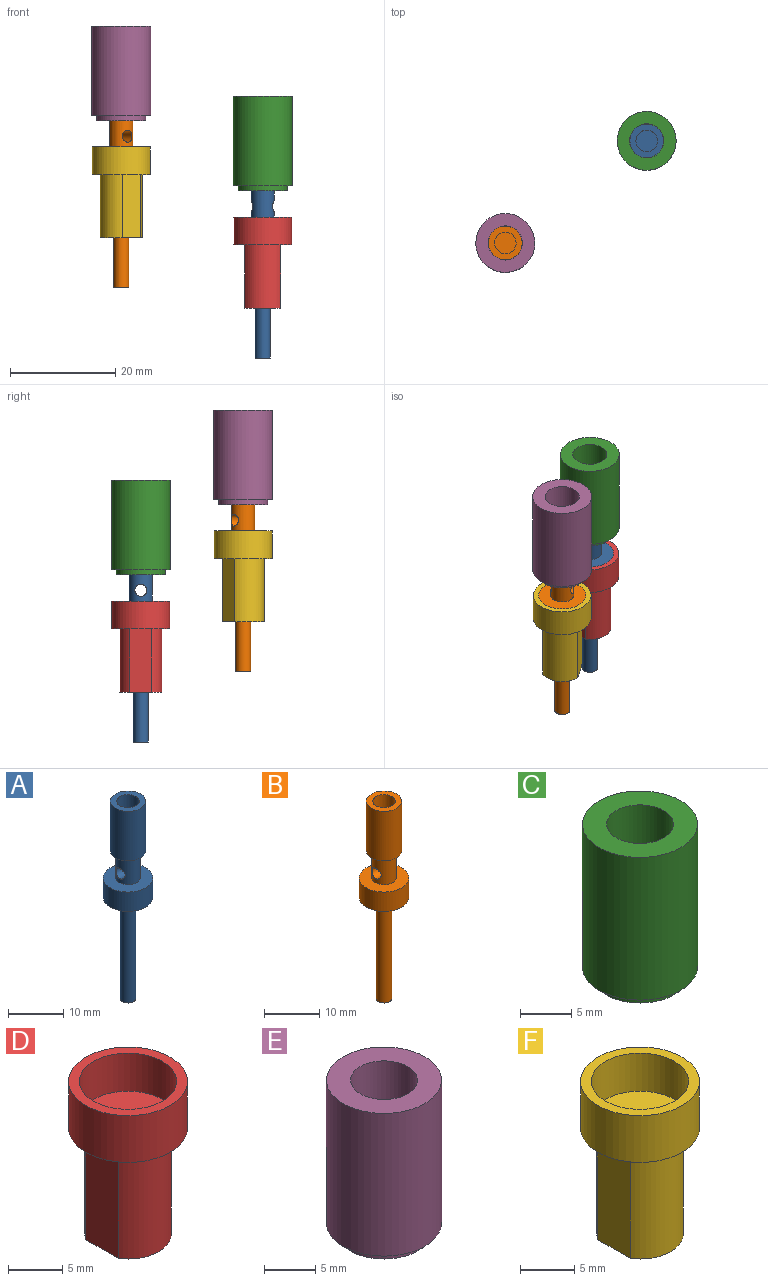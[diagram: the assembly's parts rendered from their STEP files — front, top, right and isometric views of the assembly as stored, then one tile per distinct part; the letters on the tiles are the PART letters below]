
ASSEMBLY  parts=6 mates=4
PART A: 12 faces, bbox 9x9x43.8 mm
  f0: plane 9x9mm, normal (0,0,1), area 48.4mm2, adj f1,f2
  f1: cylinder r=4.5mm len=9mm, axis (0,0,-1), area 121.6mm2, adj f0,f7
  f2: cylinder r=2.2mm len=6mm, axis (0,0,-1), area 74.3mm2, adj f0,f5,f9
  f3: cylinder r=3.2mm len=11mm, axis (0,0,-1), area 221.2mm2, adj f4,f5
  f4: plane 6.4x6.4mm, normal (0,0,1), area 19mm2, adj f3,f10
  f5: plane 6.4x6.4mm, normal (0,0,-1), area 17mm2, adj f2,f3
  f6: cylinder r=1.43mm len=22.5mm, axis (0,0,-1), area 201.5mm2, adj f7,f8
  f7: plane 9x9mm, normal (0,0,-1), area 57.2mm2, adj f1,f6
  f8: plane 2.85x2.85mm, normal (0,0,-1), area 6.4mm2, adj f6
  f9: cylinder r=1.15mm len=4.4mm, axis (1,0,0), area 29.5mm2, adj f2
  f10: cylinder r=2.05mm len=10mm, axis (0,0,1), area 128.8mm2, adj f4,f11
  f11: plane 4.1x4.1mm, normal (0,0,1), area 13.2mm2, adj f10
PART B: 12 faces, bbox 9x9x43.8 mm
  f0: plane 9x9mm, normal (0,0,1), area 48.4mm2, adj f1,f2
  f1: cylinder r=4.5mm len=9mm, axis (0,0,-1), area 121.6mm2, adj f0,f7
  f2: cylinder r=2.2mm len=6mm, axis (0,0,-1), area 74.3mm2, adj f0,f5,f9
  f3: cylinder r=3.2mm len=11mm, axis (0,0,-1), area 221.2mm2, adj f4,f5
  f4: plane 6.4x6.4mm, normal (0,0,1), area 19mm2, adj f3,f10
  f5: plane 6.4x6.4mm, normal (0,0,-1), area 17mm2, adj f2,f3
  f6: cylinder r=1.43mm len=22.5mm, axis (0,0,-1), area 201.5mm2, adj f7,f8
  f7: plane 9x9mm, normal (0,0,-1), area 57.2mm2, adj f1,f6
  f8: plane 2.85x2.85mm, normal (0,0,-1), area 6.4mm2, adj f6
  f9: cylinder r=1.15mm len=4.4mm, axis (1,0,0), area 29.5mm2, adj f2
  f10: cylinder r=2.05mm len=10mm, axis (0,0,1), area 128.8mm2, adj f4,f11
  f11: plane 4.1x4.1mm, normal (0,0,1), area 13.2mm2, adj f10
PART C: 8 faces, bbox 11.2x11.2x18 mm
  f0: plane 6.5x6.5mm, normal (0,0,1), area 18mm2, adj f1,f6
  f1: cylinder r=2.2mm len=4.4mm, axis (0,0,-1), area 13.8mm2, adj f0,f3
  f2: cylinder r=4.68mm len=9.35mm, axis (0,0,-1), area 29.4mm2, adj f3,f4
  f3: plane 9.35x9.35mm, normal (0,0,-1), area 53.5mm2, adj f1,f2
  f4: plane 11.2x11.2mm, normal (0,0,-1), area 29.9mm2, adj f2,f5
  f5: cylinder r=5.6mm len=17mm, axis (0,0,-1), area 598.2mm2, adj f4,f7
  f6: cylinder r=3.25mm len=17mm, axis (0,0,-1), area 347.1mm2, adj f0,f7
  f7: plane 11.2x11.2mm, normal (0,0,1), area 65.3mm2, adj f5,f6
PART D: 11 faces, bbox 11x11x17.3 mm
  f0: plane 11x11mm, normal (0,0,-1), area 48.2mm2, adj f2,f6,f7,f8,f9
  f1: cylinder r=4.5mm len=9mm, axis (0,0,-1), area 121.6mm2, adj f3,f5
  f2: cylinder r=5.5mm len=11mm, axis (0,0,-1), area 183.2mm2, adj f0,f3
  f3: plane 11x11mm, normal (0,0,1), area 31.4mm2, adj f1,f2
  f4: cylinder r=1.43mm len=13mm, axis (0,0,-1), area 116.4mm2, adj f5,f10
  f5: plane 9x9mm, normal (0,0,1), area 57.2mm2, adj f1,f4
  f6: plane 12x4.21mm, normal (-1,0,0), area 50.6mm2, adj f0,f7,f9,f10
  f7: cylinder r=4mm len=12mm, axis (0,0,1), area 97.5mm2, adj f0,f6,f8,f10
  f8: plane 12x4.21mm, normal (1,0,0), area 50.6mm2, adj f0,f7,f9,f10
  f9: cylinder r=4mm len=12mm, axis (0,0,1), area 97.5mm2, adj f0,f6,f8,f10
  f10: plane 8x6.8mm, normal (0,0,-1), area 40.5mm2, adj f4,f6,f7,f8,f9
PART E: 8 faces, bbox 11.2x11.2x18 mm
  f0: plane 6.5x6.5mm, normal (0,0,1), area 18mm2, adj f1,f6
  f1: cylinder r=2.2mm len=4.4mm, axis (0,0,-1), area 13.8mm2, adj f0,f3
  f2: cylinder r=4.68mm len=9.35mm, axis (0,0,-1), area 29.4mm2, adj f3,f4
  f3: plane 9.35x9.35mm, normal (0,0,-1), area 53.5mm2, adj f1,f2
  f4: plane 11.2x11.2mm, normal (0,0,-1), area 29.9mm2, adj f2,f5
  f5: cylinder r=5.6mm len=17mm, axis (0,0,-1), area 598.2mm2, adj f4,f7
  f6: cylinder r=3.25mm len=17mm, axis (0,0,-1), area 347.1mm2, adj f0,f7
  f7: plane 11.2x11.2mm, normal (0,0,1), area 65.3mm2, adj f5,f6
PART F: 11 faces, bbox 11x11x17.3 mm
  f0: plane 11x11mm, normal (0,0,-1), area 48.2mm2, adj f2,f6,f7,f8,f9
  f1: cylinder r=4.5mm len=9mm, axis (0,0,-1), area 121.6mm2, adj f3,f5
  f2: cylinder r=5.5mm len=11mm, axis (0,0,-1), area 183.2mm2, adj f0,f3
  f3: plane 11x11mm, normal (0,0,1), area 31.4mm2, adj f1,f2
  f4: cylinder r=1.43mm len=13mm, axis (0,0,-1), area 116.4mm2, adj f5,f10
  f5: plane 9x9mm, normal (0,0,1), area 57.2mm2, adj f1,f4
  f6: plane 12x4.21mm, normal (-1,0,0), area 50.6mm2, adj f0,f7,f9,f10
  f7: cylinder r=4mm len=12mm, axis (0,0,1), area 97.5mm2, adj f0,f6,f8,f10
  f8: plane 12x4.21mm, normal (1,0,0), area 50.6mm2, adj f0,f7,f9,f10
  f9: cylinder r=4mm len=12mm, axis (0,0,1), area 97.5mm2, adj f0,f6,f8,f10
  f10: plane 8x6.8mm, normal (0,0,-1), area 40.5mm2, adj f4,f6,f7,f8,f9
PLACE A t=(25.65,-11.34,-10.75)mm
PLACE B rot(axis=(0,0,-1),55deg) t=(-1.24,-10.79,2.59)mm
PLACE C t=(25.65,-11.34,-10.75)mm
PLACE D t=(25.65,-11.34,-10.75)mm
PLACE E rot(axis=(0,0,-1),55deg) t=(-1.24,-10.79,2.59)mm
PLACE F rot(axis=(0,0,-1),55deg) t=(-1.24,-10.79,2.59)mm
MATE fastened F.f1 <-> B.f1  axis (0,0,1) through (-1.24,-10.79,3.59)mm
MATE slider C.f1 <-> A.f1  axis (0,0,1) through (25.65,8.66,0.55)mm
MATE slider E.f6 <-> B.f2  axis (0,0,1) through (-1.24,-10.79,13.89)mm
MATE fastened D.f1 <-> A.f1  axis (0,0,1) through (25.65,8.66,-9.75)mm
